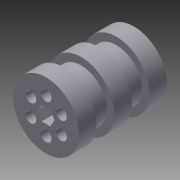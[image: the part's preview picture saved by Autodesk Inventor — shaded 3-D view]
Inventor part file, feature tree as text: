
AUTODESK INVENTOR PART (.ipt)
format: ipt  version: 2012 (Build 160160000, 160)  size: 128,000 bytes
history: native  units: in
note: dims shown in document units (in); Inventor stores cm internally (conversion verified against a paired STEP export)
features: plane x5, sketch x4, other x3
ambient origin geometry x8: Origin, YZ Plane, XZ Plane, XY Plane, X Axis, Y Axis, Z Axis, Center Point
bodies: Solid1 (feature_tree)
feature tree (12):
  other  "WheelHub.ipt"
  other  "Solid1::WheelHub.ipt"
  sketch  "Sketch1"  dims[d0=0.3937in]
  sketch  "Sketch2"
  sketch  "Sketch3"
  sketch  "Sketch4"
  plane  "Work Plane1"
  plane  "Work Plane2"
  plane  "Work Plane3"
  plane  "Work Plane4"
  plane  "Work Plane5"
  other  "TaggingFeature1"
